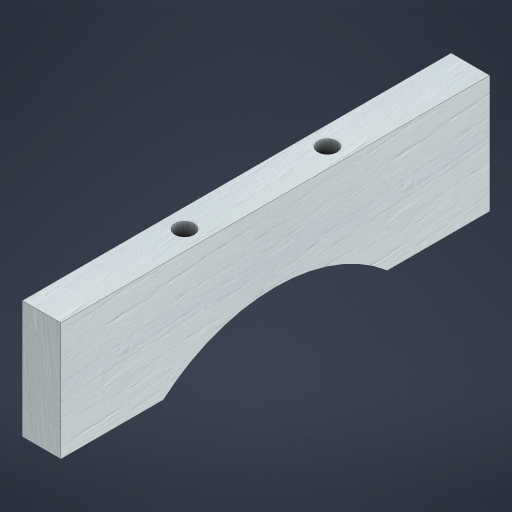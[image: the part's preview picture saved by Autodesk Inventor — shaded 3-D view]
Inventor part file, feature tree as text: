
AUTODESK INVENTOR PART (.ipt)
format: ipt  version: 2024 (Build 280153000, 153)  size: 331,776 bytes
history: native  units: mm
features: extrude x3, other x1, sketch x1
ambient origin geometry x8: Origin, YZ Plane, XZ Plane, XY Plane, X Axis, Y Axis, Z Axis, Center Point
bodies: Body1 (feature_tree)
feature tree (5):
  other  "Sólido1"
  extrude  "Extrusión1"  Depth=18.0mm
  extrude  "Extrusión2"  Depth=18.0mm
  extrude  "Extrusión3"  Depth=18.0mm
  sketch  "Boceto3"  dims[d3=0.0mm d4=9.0mm d5=9.0mm d7=66.666667mm d8=9.0mm d9=9.0mm d10=6.0mm d11=0.0mm d14=100.0mm d15=18.0mm d16=0.0mm]
